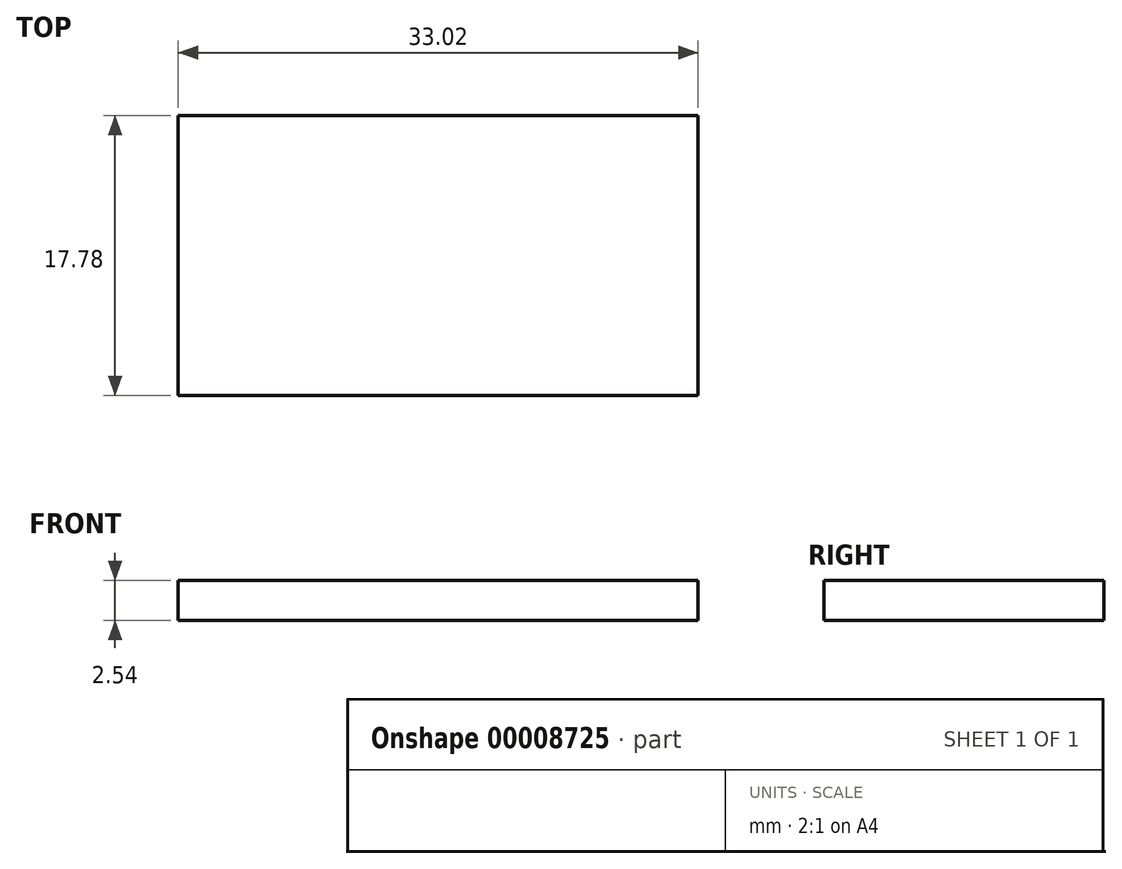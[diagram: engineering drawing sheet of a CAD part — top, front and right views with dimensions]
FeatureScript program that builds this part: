
annotation { "Feature Type Name" : "Feature", "Feature Type Description" : "" }
export const myFeature = defineFeature(function(context is Context, id is Id, definition is map)
    precondition{}
    {
        {
            var Q0;
            Q0=qCreatedBy(makeId("Top.planeOp"),FACE);
            var sketch = newSketch(context, id + "F0", { "sketchPlane" : qUnion([Q0])});
            skLineSegment(sketch, "E0.bottom", {"start": v(-13.91, 8.12) * mm, "end": v(19.1, 8.12) * mm});
            skLineSegment(sketch, "E0.top", {"start": v(-13.91, -9.66) * mm, "end": v(19.1, -9.66) * mm});
            skLineSegment(sketch, "E0.left", {"start": v(-13.91, 8.12) * mm, "end": v(-13.91, -9.66) * mm});
            skLineSegment(sketch, "E0.right", {"start": v(19.1, 8.12) * mm, "end": v(19.1, -9.66) * mm});
            skSolve(sketch);
        }
        {
            var Q0;
            Q0=makeQuery(id+"F0.imprint","IMPRINT",FACE,{"disambiguationData":[TD([[makeQuery(id+"F0.imprint","IMPRINT",EDGE,{"derivedFrom":sQuery(id+"F0.wireOp",EDGE,"E0.bottom")}),-1.0]])]});
            extrude(context, id + "F1", {"entities" : qUnion([Q0]), "depth" : 2.54 * mm});
        }
    });
